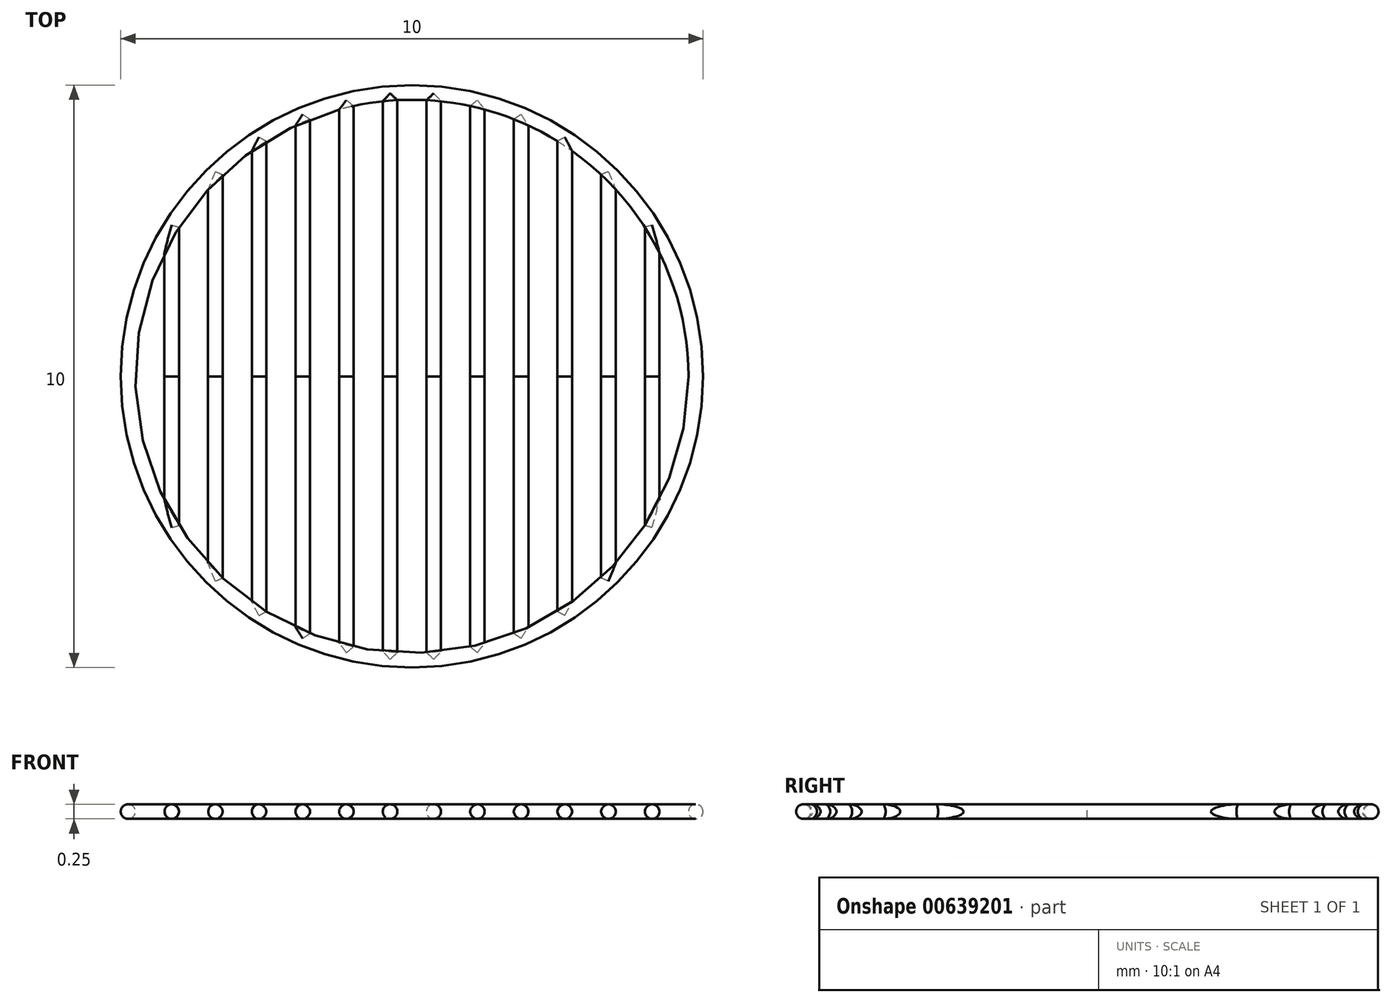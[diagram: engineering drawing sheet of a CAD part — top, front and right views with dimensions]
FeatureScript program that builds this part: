
annotation { "Feature Type Name" : "Feature", "Feature Type Description" : "" }
export const myFeature = defineFeature(function(context is Context, id is Id, definition is map)
    precondition{}
    {
        {
            assignVariable(context, id + "F0", {"name" : "d", "anyValue" : 0.25 * mm});
        }
        {
            var Q0;
            Q0=qCreatedBy(makeId("Top.planeOp"),FACE);
            cPlane(context, id + "F1", {"entities" : qUnion([Q0]), "cplaneType" : CPlaneType.OFFSET, "offset" : getVariable(context, 'd') / 2, "width" : 150 * mm, "height" : 150 * mm});
        }
        {
            var Q0;
            Q0=qCreatedBy(id+"F1.planeOp",FACE);
            var sketch = newSketch(context, id + "F2", { "sketchPlane" : qUnion([Q0])});
            skLineSegment(sketch, "E0.bottom", {"start": v(5, 5) * mm, "end": v(-5, 5) * mm, "construction": true});
            skLineSegment(sketch, "E0.top", {"start": v(5, -5) * mm, "end": v(-5, -5) * mm, "construction": true});
            skLineSegment(sketch, "E0.left", {"start": v(5, 5) * mm, "end": v(5, -5) * mm, "construction": true});
            skLineSegment(sketch, "E0.right", {"start": v(-5, 5) * mm, "end": v(-5, -5) * mm, "construction": true});
            skPoint(sketch, "E0.middle", {"position": v(0, 0) * mm});
            skCircle(sketch, "E1", {"center": v(0, 0) * mm, "radius": 4.75 * mm, "construction": true});
            skLineSegment(sketch, "E2", {"start": v(-5, 5) * mm, "end": v(-4.12, 5) * mm, "construction": true});
            skLineSegment(sketch, "E3", {"start": v(-4.12, 5) * mm, "end": v(-4.12, -5) * mm, "construction": true});
            skLineSegment(sketch, "E4", {"start": v(-4.12, -5) * mm, "end": v(-5, -5) * mm, "construction": true});
            skCircle(sketch, "E5", {"center": v(0, 0) * mm, "radius": 4.88 * mm});
            skLineSegment(sketch, "E6", {"start": v(-4.12, 5) * mm, "end": v(-3.37, 5) * mm, "construction": true});
            skLineSegment(sketch, "E7", {"start": v(-3.37, 5) * mm, "end": v(-3.37, -5) * mm, "construction": true});
            skLineSegment(sketch, "E8", {"start": v(-3.37, -5) * mm, "end": v(-4.12, -5) * mm, "construction": true});
            skLineSegment(sketch, "E9.1.0.0", {"start": v(-3.37, 5) * mm, "end": v(-2.62, 5) * mm, "construction": true});
            skLineSegment(sketch, "E9.1.0.1", {"start": v(-2.62, 5) * mm, "end": v(-2.62, -5) * mm, "construction": true});
            skLineSegment(sketch, "E9.1.0.2", {"start": v(-2.62, -5) * mm, "end": v(-3.37, -5) * mm, "construction": true});
            skLineSegment(sketch, "E9.2.0.0", {"start": v(-2.62, 5) * mm, "end": v(-1.87, 5) * mm, "construction": true});
            skLineSegment(sketch, "E9.2.0.1", {"start": v(-1.87, 5) * mm, "end": v(-1.87, -5) * mm, "construction": true});
            skLineSegment(sketch, "E9.2.0.2", {"start": v(-1.87, -5) * mm, "end": v(-2.62, -5) * mm, "construction": true});
            skLineSegment(sketch, "E9.3.0.0", {"start": v(-1.87, 5) * mm, "end": v(-1.12, 5) * mm, "construction": true});
            skLineSegment(sketch, "E9.3.0.1", {"start": v(-1.12, 5) * mm, "end": v(-1.12, -5) * mm, "construction": true});
            skLineSegment(sketch, "E9.3.0.2", {"start": v(-1.12, -5) * mm, "end": v(-1.87, -5) * mm, "construction": true});
            skLineSegment(sketch, "E9.4.0.0", {"start": v(-1.12, 5) * mm, "end": v(-0.37, 5) * mm, "construction": true});
            skLineSegment(sketch, "E9.4.0.1", {"start": v(-0.37, 5) * mm, "end": v(-0.37, -5) * mm, "construction": true});
            skLineSegment(sketch, "E9.4.0.2", {"start": v(-0.37, -5) * mm, "end": v(-1.12, -5) * mm, "construction": true});
            skLineSegment(sketch, "E9.5.0.0", {"start": v(-0.37, 5) * mm, "end": v(0.38, 5) * mm, "construction": true});
            skLineSegment(sketch, "E9.5.0.1", {"start": v(0.38, 5) * mm, "end": v(0.38, -5) * mm, "construction": true});
            skLineSegment(sketch, "E9.5.0.2", {"start": v(0.38, -5) * mm, "end": v(-0.37, -5) * mm, "construction": true});
            skLineSegment(sketch, "E9.6.0.0", {"start": v(0.38, 5) * mm, "end": v(1.13, 5) * mm, "construction": true});
            skLineSegment(sketch, "E9.6.0.1", {"start": v(1.13, 5) * mm, "end": v(1.13, -5) * mm, "construction": true});
            skLineSegment(sketch, "E9.6.0.2", {"start": v(1.13, -5) * mm, "end": v(0.38, -5) * mm, "construction": true});
            skLineSegment(sketch, "E9.7.0.0", {"start": v(1.13, 5) * mm, "end": v(1.88, 5) * mm, "construction": true});
            skLineSegment(sketch, "E9.7.0.1", {"start": v(1.88, 5) * mm, "end": v(1.88, -5) * mm, "construction": true});
            skLineSegment(sketch, "E9.7.0.2", {"start": v(1.88, -5) * mm, "end": v(1.13, -5) * mm, "construction": true});
            skLineSegment(sketch, "E9.8.0.0", {"start": v(1.88, 5) * mm, "end": v(2.62, 5) * mm, "construction": true});
            skLineSegment(sketch, "E9.8.0.1", {"start": v(2.62, 5) * mm, "end": v(2.62, -5) * mm, "construction": true});
            skLineSegment(sketch, "E9.8.0.2", {"start": v(2.62, -5) * mm, "end": v(1.88, -5) * mm, "construction": true});
            skLineSegment(sketch, "E9.9.0.0", {"start": v(2.62, 5) * mm, "end": v(3.37, 5) * mm, "construction": true});
            skLineSegment(sketch, "E9.9.0.1", {"start": v(3.37, 5) * mm, "end": v(3.37, -5) * mm, "construction": true});
            skLineSegment(sketch, "E9.9.0.2", {"start": v(3.37, -5) * mm, "end": v(2.62, -5) * mm, "construction": true});
            skLineSegment(sketch, "E9.10.0.0", {"start": v(3.37, 5) * mm, "end": v(4.12, 5) * mm, "construction": true});
            skLineSegment(sketch, "E9.10.0.1", {"start": v(4.12, 5) * mm, "end": v(4.12, -5) * mm, "construction": true});
            skLineSegment(sketch, "E9.10.0.2", {"start": v(4.12, -5) * mm, "end": v(3.37, -5) * mm, "construction": true});
            skLineSegment(sketch, "E10", {"start": v(4.12, 5) * mm, "end": v(5, 5) * mm, "construction": true});
            skLineSegment(sketch, "E11", {"start": v(4.12, -5) * mm, "end": v(5, -5) * mm, "construction": true});
            skSolve(sketch);
        }
        {
            var Q0;
            Q0=qCreatedBy(makeId("Front.planeOp"),FACE);
            var sketch = newSketch(context, id + "F3", { "sketchPlane" : qUnion([Q0])});
            skCircle(sketch, "E12", {"center": v(-4.88, 0.12) * mm, "radius": 0.13 * mm});
            skSolve(sketch);
        }
        {
            var Q0;
            Q0=qCreatedBy(makeId("Front.planeOp"),FACE);
            var sketch = newSketch(context, id + "F4", { "sketchPlane" : qUnion([Q0])});
            skCircle(sketch, "E13", {"center": v(-4.12, 0.12) * mm, "radius": 0.13 * mm});
            skCircle(sketch, "E14", {"center": v(-3.37, 0.12) * mm, "radius": 0.13 * mm});
            skCircle(sketch, "E15", {"center": v(-2.62, 0.12) * mm, "radius": 0.13 * mm});
            skCircle(sketch, "E16", {"center": v(-1.87, 0.12) * mm, "radius": 0.13 * mm});
            skCircle(sketch, "E17", {"center": v(-1.12, 0.12) * mm, "radius": 0.13 * mm});
            skCircle(sketch, "E18", {"center": v(-0.37, 0.12) * mm, "radius": 0.13 * mm});
            skCircle(sketch, "E19", {"center": v(1.13, 0.12) * mm, "radius": 0.13 * mm});
            skCircle(sketch, "E20", {"center": v(1.88, 0.12) * mm, "radius": 0.13 * mm});
            skCircle(sketch, "E21", {"center": v(2.62, 0.12) * mm, "radius": 0.13 * mm});
            skCircle(sketch, "E22", {"center": v(3.37, 0.12) * mm, "radius": 0.13 * mm});
            skCircle(sketch, "E23", {"center": v(4.12, 0.12) * mm, "radius": 0.13 * mm});
            skCircle(sketch, "E24", {"center": v(0.38, 0.12) * mm, "radius": 0.13 * mm});
            skSolve(sketch);
        }
        {
            var Q0;
            Q0=makeQuery(id+"F3.imprint","IMPRINT",FACE,{"disambiguationData":[TD([[makeQuery(id+"F3.imprint","IMPRINT",EDGE,{"derivedFrom":sQuery(id+"F3.wireOp",EDGE,"E12")}),1.0]])]});
            var Q1;
            Q1=sQuery(id+"F2.wireOp",EDGE,"E5");
            sweep(context, id + "F5", {"profiles" : qUnion([Q0]), "path" : qUnion([Q1])});
        }
        {
            var Q0;
            Q0 = qSketchRegion(id + "F4", true);
            extrude(context, id + "F6", {"entities" : qUnion([Q0]), "endBound" : BoundingType.UP_TO_NEXT, "depth" : 25 * mm, "offsetDistance" : 25 * mm});
        }
        {
            var Q0;
            Q0 = qSketchRegion(id + "F4", true);
            extrude(context, id + "F7", {"entities" : qUnion([Q0]), "endBound" : BoundingType.UP_TO_NEXT, "oppositeDirection" : true, "depth" : 25 * mm, "offsetDistance" : 25 * mm});
        }
    });
